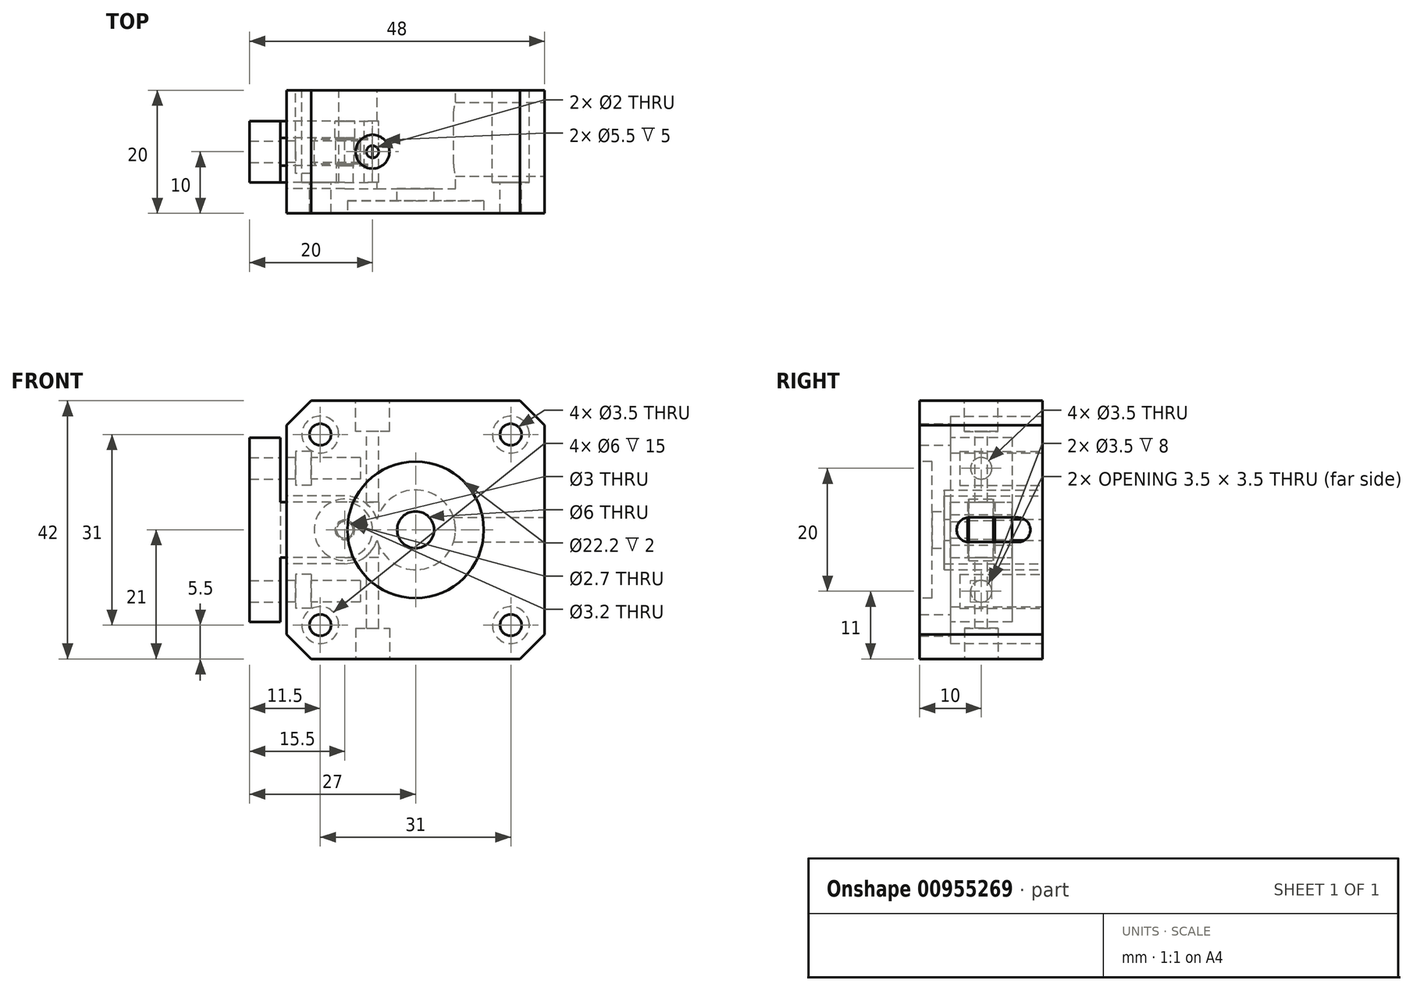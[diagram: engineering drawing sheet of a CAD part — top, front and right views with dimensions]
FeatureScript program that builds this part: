
annotation { "Feature Type Name" : "Feature", "Feature Type Description" : "" }
export const myFeature = defineFeature(function(context is Context, id is Id, definition is map)
    precondition{}
    {
        {
            var Q0;
            Q0=qCreatedBy(makeId("Front.planeOp"),FACE);
            var sketch = newSketch(context, id + "F0", { "sketchPlane" : qUnion([Q0])});
            skLineSegment(sketch, "E0.bottom", {"start": v(21, -21) * mm, "end": v(-21, -21) * mm});
            skLineSegment(sketch, "E0.top", {"start": v(21, 21) * mm, "end": v(-21, 21) * mm});
            skLineSegment(sketch, "E0.left", {"start": v(21, -21) * mm, "end": v(21, 21) * mm});
            skLineSegment(sketch, "E0.right", {"start": v(-21, -21) * mm, "end": v(-21, 21) * mm});
            skPoint(sketch, "E0.middle", {"position": v(0, 0) * mm});
            skLineSegment(sketch, "E1.bottom", {"start": v(15.5, -15.5) * mm, "end": v(-15.5, -15.5) * mm, "construction": true});
            skLineSegment(sketch, "E1.top", {"start": v(15.5, 15.5) * mm, "end": v(-15.5, 15.5) * mm, "construction": true});
            skLineSegment(sketch, "E1.left", {"start": v(15.5, -15.5) * mm, "end": v(15.5, 15.5) * mm, "construction": true});
            skLineSegment(sketch, "E1.right", {"start": v(-15.5, -15.5) * mm, "end": v(-15.5, 15.5) * mm, "construction": true});
            skCircle(sketch, "E2", {"center": v(-15.5, 15.5) * mm, "radius": 1.75 * mm});
            skCircle(sketch, "E3", {"center": v(15.5, 15.5) * mm, "radius": 1.75 * mm});
            skCircle(sketch, "E4", {"center": v(-15.5, -15.5) * mm, "radius": 1.75 * mm});
            skCircle(sketch, "E5", {"center": v(15.5, -15.5) * mm, "radius": 1.75 * mm});
            skCircle(sketch, "E6", {"center": v(0, 0) * mm, "radius": 3 * mm});
            skSolve(sketch);
        }
        {
            var Q0;
            Q0 = qSketchRegion(id + "F0", true);
            extrude(context, id + "F1", {"entities" : qUnion([Q0]), "endBound" : BoundingType.SYMMETRIC, "depth" : 20 * mm, "offsetDistance" : 25 * mm});
        }
        {
            var Q0;
            Q0=makeQuery(id+"F1.opExtrude","CAP_FACE",FACE,{"disambiguationData":[OSD([sQuery(id+"F0.wireOp",EDGE,"E0.bottom"),sQuery(id+"F0.wireOp",EDGE,"E0.top"),sQuery(id+"F0.wireOp",EDGE,"E0.left"),sQuery(id+"F0.wireOp",EDGE,"E0.right"),sQuery(id+"F0.wireOp",EDGE,"E2"),sQuery(id+"F0.wireOp",EDGE,"E3"),sQuery(id+"F0.wireOp",EDGE,"E4"),sQuery(id+"F0.wireOp",EDGE,"E5"),sQuery(id+"F0.wireOp",EDGE,"E6")])],"isStart":false});
            var sketch = newSketch(context, id + "F2", { "sketchPlane" : qUnion([Q0])});
            skCircle(sketch, "E7", {"center": v(0, 0) * mm, "radius": 11.1 * mm});
            skSolve(sketch);
        }
        {
            var Q0;
            Q0 = qSketchRegion(id + "F2", true);
            extrude(context, id + "F3", {"entities" : qUnion([Q0]), "operationType" : NewBodyOperationType.REMOVE, "oppositeDirection" : true, "depth" : 2 * mm, "offsetDistance" : 25 * mm});
        }
        {
            var Q0;
            Q0=makeQuery(id+"F1.opExtrude","SWEPT_FACE",FACE,{"disambiguationData":[OSD([sQuery(id+"F0.wireOp",EDGE,"E0.top")])]});
            var sketch = newSketch(context, id + "F4", { "sketchPlane" : qUnion([Q0])});
            skLineSegment(sketch, "E8", {"start": v(21, 10) * mm, "end": v(-21, -10) * mm, "construction": true});
            skLineSegment(sketch, "E9", {"start": v(0, 0) * mm, "end": v(-7, 0) * mm, "construction": true});
            skCircle(sketch, "E10", {"center": v(-7, 0) * mm, "radius": 1 * mm});
            skSolve(sketch);
        }
        {
            var Q0;
            Q0 = qSketchRegion(id + "F4", true);
            var Q1;
            Q1=makeQuery(id+"F1.opExtrude","SWEPT_FACE",FACE,{"disambiguationData":[OSD([sQuery(id+"F0.wireOp",EDGE,"E0.bottom")])]});
            extrude(context, id + "F5", {"entities" : qUnion([Q0]), "operationType" : NewBodyOperationType.REMOVE, "endBound" : BoundingType.UP_TO_SURFACE, "oppositeDirection" : true, "depth" : 25 * mm, "endBoundEntityFace" : qUnion([Q1]), "offsetDistance" : 25 * mm});
        }
        {
            var Q0;
            Q0=makeQuery(id+"F1.opExtrude","CAP_FACE",FACE,{"disambiguationData":[OSD([sQuery(id+"F0.wireOp",EDGE,"E0.bottom"),sQuery(id+"F0.wireOp",EDGE,"E0.top"),sQuery(id+"F0.wireOp",EDGE,"E0.left"),sQuery(id+"F0.wireOp",EDGE,"E0.right"),sQuery(id+"F0.wireOp",EDGE,"E2"),sQuery(id+"F0.wireOp",EDGE,"E3"),sQuery(id+"F0.wireOp",EDGE,"E4"),sQuery(id+"F0.wireOp",EDGE,"E5"),sQuery(id+"F0.wireOp",EDGE,"E6")])],"isStart":true});
            var sketch = newSketch(context, id + "F6", { "sketchPlane" : qUnion([Q0])});
            skCircle(sketch, "E11", {"center": v(0, 0) * mm, "radius": 6 * mm, "construction": true});
            skLineSegment(sketch, "E12", {"start": v(0, 0) * mm, "end": v(21, 0) * mm, "construction": true});
            skCircle(sketch, "E13", {"center": v(11.5, 0) * mm, "radius": 5 * mm, "construction": true});
            skArc(sketch, "E14.0", {"start": v(6.27, 1.7) * mm, "mid": v(-6.5, 0) * mm, "end": v(6.27, -1.7) * mm});
            skArc(sketch, "E15.0", {"start": v(11.5, 5.5) * mm, "mid": v(8.27, 4.45) * mm, "end": v(6.27, 1.7) * mm});
            skLineSegment(sketch, "E16", {"start": v(11.5, 5.5) * mm, "end": v(21, 5.5) * mm});
            skLineSegment(sketch, "E17", {"start": v(11.5, -5.5) * mm, "end": v(21, -5.5) * mm});
            skLineSegment(sketch, "E18", {"start": v(21, -5.5) * mm, "end": v(21, 5.5) * mm});
            skArc(sketch, "E19.trimOffspring", {"start": v(6.27, -1.7) * mm, "mid": v(8.27, -4.45) * mm, "end": v(11.5, -5.5) * mm});
            skSolve(sketch);
        }
        {
            var Q0;
            Q0 = qSketchRegion(id + "F6", true);
            extrude(context, id + "F7", {"entities" : qUnion([Q0]), "operationType" : NewBodyOperationType.REMOVE, "oppositeDirection" : true, "depth" : 16 * mm, "offsetDistance" : 25 * mm});
        }
        {
            var Q0;
            Q0=makeQuery(id+"F1.opExtrude","SWEPT_FACE",FACE,{"disambiguationData":[OSD([sQuery(id+"F0.wireOp",EDGE,"E0.right")])]});
            var sketch = newSketch(context, id + "F8", { "sketchPlane" : qUnion([Q0])});
            skCircle(sketch, "E20", {"center": v(0, 10) * mm, "radius": 1.75 * mm});
            skCircle(sketch, "E21", {"center": v(0, -10) * mm, "radius": 1.75 * mm});
            skLineSegment(sketch, "E22", {"start": v(0, 21) * mm, "end": v(0, 10) * mm, "construction": true});
            skLineSegment(sketch, "E23", {"start": v(0, 10) * mm, "end": v(0, -10) * mm, "construction": true});
            skLineSegment(sketch, "E24", {"start": v(0, -10) * mm, "end": v(0, -21) * mm, "construction": true});
            skSolve(sketch);
        }
        {
            var Q0;
            Q0 = qSketchRegion(id + "F8", true);
            var Q1;
            Q1=makeQuery(id+"F1.opExtrude","SWEPT_FACE",FACE,{"disambiguationData":[OSD([sQuery(id+"F0.wireOp",EDGE,"E0.left")])]});
            extrude(context, id + "F9", {"entities" : qUnion([Q0]), "operationType" : NewBodyOperationType.REMOVE, "oppositeDirection" : true, "depth" : 12 * mm, "endBoundEntityFace" : qUnion([Q1]), "offsetDistance" : 25 * mm});
        }
        {
            var Q0;
            Q0=qCreatedBy(makeId("Front.planeOp"),FACE);
            var sketch = newSketch(context, id + "F10", { "sketchPlane" : qUnion([Q0])});
            skCircle(sketch, "E25", {"center": v(-11.5, 0) * mm, "radius": 5 * mm});
            skCircle(sketch, "E26", {"center": v(-11.5, 0) * mm, "radius": 1.5 * mm});
            skSolve(sketch);
        }
        {
            var Q0;
            Q0 = qSketchRegion(id + "F10", true);
            extrude(context, id + "F11", {"entities" : qUnion([Q0]), "operationType" : NewBodyOperationType.ADD, "endBound" : BoundingType.SYMMETRIC, "depth" : 4 * mm, "offsetDistance" : 25 * mm});
        }
        {
            var Q0;
            Q0=makeQuery(id+"F1.opExtrude","SWEPT_FACE",FACE,{"disambiguationData":[OSD([sQuery(id+"F0.wireOp",EDGE,"E0.right")])]});
            cPlane(context, id + "F12", {"entities" : qUnion([Q0]), "cplaneType" : CPlaneType.OFFSET, "offset" : 1 * mm, "width" : 150 * mm, "height" : 150 * mm});
        }
        {
            var Q0;
            Q0=qCreatedBy(id+"F12.planeOp",FACE);
            var sketch = newSketch(context, id + "F13", { "sketchPlane" : qUnion([Q0])});
            skCircle(sketch, "E27", {"center": v(0, 10) * mm, "radius": 1.75 * mm});
            skCircle(sketch, "E28", {"center": v(0, -10) * mm, "radius": 1.75 * mm});
            skLineSegment(sketch, "E29.bottom", {"start": v(-5, 15) * mm, "end": v(5, 15) * mm});
            skLineSegment(sketch, "E29.top", {"start": v(-5, -15) * mm, "end": v(5, -15) * mm});
            skLineSegment(sketch, "E29.left", {"start": v(-5, 15) * mm, "end": v(-5, -15) * mm});
            skLineSegment(sketch, "E29.right", {"start": v(5, 15) * mm, "end": v(5, -15) * mm});
            skSolve(sketch);
        }
        {
            var Q0;
            Q0 = qSketchRegion(id + "F13", true);
            extrude(context, id + "F14", {"entities" : qUnion([Q0]), "depth" : 5 * mm, "offsetDistance" : 25 * mm});
        }
        {
            var Q0;
            Q0=makeQuery(id+"F14.opExtrude","CAP_FACE",FACE,{"disambiguationData":[OSD([sQuery(id+"F13.wireOp",EDGE,"E27"),sQuery(id+"F13.wireOp",EDGE,"E28"),sQuery(id+"F13.wireOp",EDGE,"E29.bottom"),sQuery(id+"F13.wireOp",EDGE,"E29.top"),sQuery(id+"F13.wireOp",EDGE,"E29.left"),sQuery(id+"F13.wireOp",EDGE,"E29.right")])],"isStart":true});
            var sketch = newSketch(context, id + "F15", { "sketchPlane" : qUnion([Q0])});
            skLineSegment(sketch, "E30", {"start": v(-5, 15) * mm, "end": v(5, -15) * mm, "construction": true});
            skLineSegment(sketch, "E31.bottom", {"start": v(-5, 4.5) * mm, "end": v(-2.25, 4.5) * mm});
            skLineSegment(sketch, "E31.top", {"start": v(-5, -4.5) * mm, "end": v(-2.25, -4.5) * mm});
            skLineSegment(sketch, "E31.left", {"start": v(-5, 4.5) * mm, "end": v(-5, -4.5) * mm});
            skLineSegment(sketch, "E31.right", {"start": v(-2.25, 4.5) * mm, "end": v(-2.25, -4.5) * mm});
            skLineSegment(sketch, "E32.bottom", {"start": v(2.25, 4.5) * mm, "end": v(5, 4.5) * mm});
            skLineSegment(sketch, "E32.top", {"start": v(2.25, -4.5) * mm, "end": v(5, -4.5) * mm});
            skLineSegment(sketch, "E32.left", {"start": v(2.25, 4.5) * mm, "end": v(2.25, -4.5) * mm});
            skLineSegment(sketch, "E32.right", {"start": v(5, 4.5) * mm, "end": v(5, -4.5) * mm});
            skLineSegment(sketch, "E33", {"start": v(0, 0) * mm, "end": v(-2.25, 0) * mm, "construction": true});
            skLineSegment(sketch, "E34", {"start": v(0, 0) * mm, "end": v(2.25, 0) * mm, "construction": true});
            skSolve(sketch);
        }
        {
            var Q0;
            Q0 = qSketchRegion(id + "F15", true);
            extrude(context, id + "F16", {"entities" : qUnion([Q0]), "operationType" : NewBodyOperationType.ADD, "depth" : 16 * mm, "offsetDistance" : 25 * mm});
        }
        {
            var Q0;
            Q0=makeQuery(id+"F16.boolean.opBoolean","MERGE",FACE,{"derivedFrom":[makeQuery(id+"F14.opExtrude","SWEPT_FACE",FACE,{"disambiguationData":[OSD([sQuery(id+"F13.wireOp",EDGE,"E29.left")])]}),makeQuery(id+"F16.opExtrude","SWEPT_FACE",FACE,{"disambiguationData":[OSD([sQuery(id+"F15.wireOp",EDGE,"E32.right")])]})]});
            var sketch = newSketch(context, id + "F17", { "sketchPlane" : qUnion([Q0])});
            skArc(sketch, "E35", {"start": v(11.5, 4.5) * mm, "mid": v(7, 0) * mm, "end": v(11.5, -4.5) * mm});
            skLineSegment(sketch, "E36", {"start": v(11.5, 4.5) * mm, "end": v(6, 4.5) * mm});
            skLineSegment(sketch, "E37", {"start": v(6, 4.5) * mm, "end": v(6, -4.5) * mm});
            skLineSegment(sketch, "E38", {"start": v(6, -4.5) * mm, "end": v(11.5, -4.5) * mm});
            skSolve(sketch);
        }
        {
            var Q0;
            Q0 = qSketchRegion(id + "F17", true);
            var Q1;
            Q1=makeQuery(id+"F16.boolean.opBoolean","MERGE",FACE,{"derivedFrom":[makeQuery(id+"F14.opExtrude","SWEPT_FACE",FACE,{"disambiguationData":[OSD([sQuery(id+"F13.wireOp",EDGE,"E29.right")])]}),makeQuery(id+"F16.opExtrude","SWEPT_FACE",FACE,{"disambiguationData":[OSD([sQuery(id+"F15.wireOp",EDGE,"E31.left")])]})]});
            extrude(context, id + "F18", {"entities" : qUnion([Q0]), "operationType" : NewBodyOperationType.REMOVE, "endBound" : BoundingType.UP_TO_SURFACE, "oppositeDirection" : true, "depth" : 25 * mm, "endBoundEntityFace" : qUnion([Q1]), "offsetDistance" : 25 * mm});
        }
        {
            var Q0;
            Q0=makeQuery(id+"F1.opExtrude","SWEPT_FACE",FACE,{"disambiguationData":[OSD([sQuery(id+"F0.wireOp",EDGE,"E0.top")])]});
            var sketch = newSketch(context, id + "F19", { "sketchPlane" : qUnion([Q0])});
            skCircle(sketch, "E39", {"center": v(-7, 0) * mm, "radius": 2.75 * mm});
            skSolve(sketch);
        }
        {
            var Q0;
            Q0 = qSketchRegion(id + "F19", true);
            extrude(context, id + "F20", {"entities" : qUnion([Q0]), "operationType" : NewBodyOperationType.REMOVE, "oppositeDirection" : true, "depth" : 5 * mm, "offsetDistance" : 25 * mm});
        }
        {
            var Q0;
            Q0=makeQuery(id+"F1.opExtrude","SWEPT_FACE",FACE,{"disambiguationData":[OSD([sQuery(id+"F0.wireOp",EDGE,"E0.bottom")])]});
            var sketch = newSketch(context, id + "F21", { "sketchPlane" : qUnion([Q0])});
            skCircle(sketch, "E40", {"center": v(-7, 0) * mm, "radius": 2.75 * mm});
            skSolve(sketch);
        }
        {
            var Q0;
            Q0 = qSketchRegion(id + "F21", true);
            extrude(context, id + "F22", {"entities" : qUnion([Q0]), "operationType" : NewBodyOperationType.REMOVE, "oppositeDirection" : true, "depth" : 5 * mm, "offsetDistance" : 25 * mm});
        }
        {
            var Q0;
            Q0=makeQuery(id+"F16.boolean.opBoolean","MERGE",FACE,{"derivedFrom":[makeQuery(id+"F14.opExtrude","SWEPT_FACE",FACE,{"disambiguationData":[OSD([sQuery(id+"F13.wireOp",EDGE,"E29.left")])]}),makeQuery(id+"F16.opExtrude","SWEPT_FACE",FACE,{"disambiguationData":[OSD([sQuery(id+"F15.wireOp",EDGE,"E32.right")])]})]});
            var sketch = newSketch(context, id + "F23", { "sketchPlane" : qUnion([Q0])});
            skCircle(sketch, "E41", {"center": v(11.5, 0) * mm, "radius": 1.35 * mm});
            skSolve(sketch);
        }
        {
            var Q0;
            Q0 = qSketchRegion(id + "F23", true);
            var Q1;
            Q1=makeQuery(id+"F16.boolean.opBoolean","MERGE",FACE,{"derivedFrom":[makeQuery(id+"F14.opExtrude","SWEPT_FACE",FACE,{"disambiguationData":[OSD([sQuery(id+"F13.wireOp",EDGE,"E29.right")])]}),makeQuery(id+"F16.opExtrude","SWEPT_FACE",FACE,{"disambiguationData":[OSD([sQuery(id+"F15.wireOp",EDGE,"E31.left")])]})]});
            extrude(context, id + "F24", {"entities" : qUnion([Q0]), "operationType" : NewBodyOperationType.REMOVE, "endBound" : BoundingType.UP_TO_SURFACE, "oppositeDirection" : true, "depth" : 25 * mm, "endBoundEntityFace" : qUnion([Q1]), "offsetDistance" : 25 * mm});
        }
        {
            var Q0;
            Q0=makeQuery(id+"F16.boolean.opBoolean","MERGE",FACE,{"derivedFrom":[makeQuery(id+"F14.opExtrude","SWEPT_FACE",FACE,{"disambiguationData":[OSD([sQuery(id+"F13.wireOp",EDGE,"E29.left")])]}),makeQuery(id+"F16.opExtrude","SWEPT_FACE",FACE,{"disambiguationData":[OSD([sQuery(id+"F15.wireOp",EDGE,"E32.right")])]})]});
            var sketch = newSketch(context, id + "F25", { "sketchPlane" : qUnion([Q0])});
            skCircle(sketch, "E42", {"center": v(11.5, 0) * mm, "radius": 1.6 * mm});
            skSolve(sketch);
        }
        {
            var Q0;
            Q0 = qSketchRegion(id + "F25", true);
            var Q1;
            Q1=makeQuery(id+"F16.opExtrude","SWEPT_FACE",FACE,{"disambiguationData":[OSD([sQuery(id+"F15.wireOp",EDGE,"E32.left")])]});
            extrude(context, id + "F26", {"entities" : qUnion([Q0]), "operationType" : NewBodyOperationType.REMOVE, "endBound" : BoundingType.UP_TO_SURFACE, "oppositeDirection" : true, "depth" : 25 * mm, "endBoundEntityFace" : qUnion([Q1]), "offsetDistance" : 25 * mm});
        }
        {
            var Q0;
            Q0=makeQuery(id+"F1.opExtrude","SWEPT_EDGE",EDGE,{"disambiguationData":[OSD([sQuery(id+"F0.wireOp",EDGE,"E0.top"),sQuery(id+"F0.wireOp",EDGE,"E0.left")])]});
            var Q1;
            Q1=makeQuery(id+"F1.opExtrude","SWEPT_EDGE",EDGE,{"disambiguationData":[OSD([sQuery(id+"F0.wireOp",EDGE,"E0.bottom"),sQuery(id+"F0.wireOp",EDGE,"E0.left")])]});
            var Q2;
            Q2=makeQuery(id+"F1.opExtrude","SWEPT_EDGE",EDGE,{"disambiguationData":[OSD([sQuery(id+"F0.wireOp",EDGE,"E0.bottom"),sQuery(id+"F0.wireOp",EDGE,"E0.right")])]});
            var Q3;
            Q3=makeQuery(id+"F1.opExtrude","SWEPT_EDGE",EDGE,{"disambiguationData":[OSD([sQuery(id+"F0.wireOp",EDGE,"E0.top"),sQuery(id+"F0.wireOp",EDGE,"E0.right")])]});
            chamfer(context, id + "F27", {"entities" : qUnion([Q0, Q1, Q2, Q3]), "width" : 4 * mm, "tangentPropagation" : true});
        }
        {
            var Q0;
            Q0=makeQuery(id+"F1.opExtrude","CAP_FACE",FACE,{"disambiguationData":[OSD([sQuery(id+"F0.wireOp",EDGE,"E0.bottom"),sQuery(id+"F0.wireOp",EDGE,"E0.top"),sQuery(id+"F0.wireOp",EDGE,"E0.left"),sQuery(id+"F0.wireOp",EDGE,"E0.right"),sQuery(id+"F0.wireOp",EDGE,"E2"),sQuery(id+"F0.wireOp",EDGE,"E3"),sQuery(id+"F0.wireOp",EDGE,"E4"),sQuery(id+"F0.wireOp",EDGE,"E5"),sQuery(id+"F0.wireOp",EDGE,"E6")])],"isStart":true});
            var sketch = newSketch(context, id + "F28", { "sketchPlane" : qUnion([Q0])});
            skLineSegment(sketch, "E43.bottom", {"start": v(17, 12.75) * mm, "end": v(19.5, 12.75) * mm});
            skLineSegment(sketch, "E43.top", {"start": v(17, 7.25) * mm, "end": v(19.5, 7.25) * mm});
            skLineSegment(sketch, "E43.left", {"start": v(17, 12.75) * mm, "end": v(17, 7.25) * mm});
            skLineSegment(sketch, "E43.right", {"start": v(19.5, 12.75) * mm, "end": v(19.5, 7.25) * mm});
            skLineSegment(sketch, "E44", {"start": v(17, 7.25) * mm, "end": v(19.5, 12.75) * mm, "construction": true});
            skLineSegment(sketch, "E45.bottom", {"start": v(17, -7.25) * mm, "end": v(19.5, -7.25) * mm});
            skLineSegment(sketch, "E45.top", {"start": v(17, -12.75) * mm, "end": v(19.5, -12.75) * mm});
            skLineSegment(sketch, "E45.left", {"start": v(17, -7.25) * mm, "end": v(17, -12.75) * mm});
            skLineSegment(sketch, "E45.right", {"start": v(19.5, -7.25) * mm, "end": v(19.5, -12.75) * mm});
            skLineSegment(sketch, "E46", {"start": v(17, -12.75) * mm, "end": v(19.5, -7.25) * mm, "construction": true});
            skLineSegment(sketch, "E47", {"start": v(18.25, -10) * mm, "end": v(18.25, 10) * mm, "construction": true});
            skLineSegment(sketch, "E48", {"start": v(21, -17) * mm, "end": v(19.5, -12.75) * mm, "construction": true});
            skLineSegment(sketch, "E49", {"start": v(21, 17) * mm, "end": v(19.5, 12.75) * mm, "construction": true});
            skSolve(sketch);
        }
        {
            var Q0;
            Q0 = qSketchRegion(id + "F28", true);
            extrude(context, id + "F29", {"entities" : qUnion([Q0]), "operationType" : NewBodyOperationType.REMOVE, "oppositeDirection" : true, "depth" : 13.5 * mm, "offsetDistance" : 25 * mm});
        }
        {
            var Q0;
            Q0=makeQuery(id+"F1.opExtrude","SWEPT_FACE",FACE,{"disambiguationData":[OSD([sQuery(id+"F0.wireOp",EDGE,"E0.left")])]});
            var sketch = newSketch(context, id + "F30", { "sketchPlane" : qUnion([Q0])});
            skLineSegment(sketch, "E50", {"start": v(-10, 0) * mm, "end": v(-2, 0) * mm, "construction": true});
            skLineSegment(sketch, "E51", {"start": v(-2, 0) * mm, "end": v(6, 0) * mm, "construction": true});
            skLineSegment(sketch, "E52", {"start": v(6, 0) * mm, "end": v(10, 0) * mm, "construction": true});
            skArc(sketch, "E53", {"start": v(-2, 2) * mm, "mid": v(-4, 0) * mm, "end": v(-2, -2) * mm});
            skArc(sketch, "E54", {"start": v(6, -2) * mm, "mid": v(8, 0) * mm, "end": v(6, 2) * mm});
            skLineSegment(sketch, "E55", {"start": v(-2, 2) * mm, "end": v(6, 2) * mm});
            skLineSegment(sketch, "E56", {"start": v(-2, -2) * mm, "end": v(6, -2) * mm});
            skSolve(sketch);
        }
        {
            var Q0;
            Q0 = qSketchRegion(id + "F30", true);
            var Q1;
            Q1=makeQuery(id+"F7.boolean.opBoolean","COPY",FACE,{"derivedFrom":makeQuery(id+"F7.opExtrude","SWEPT_FACE",FACE,{"disambiguationData":[OSD([sQuery(id+"F6.wireOp",EDGE,"E14.0")])]})});
            extrude(context, id + "F31", {"entities" : qUnion([Q0]), "operationType" : NewBodyOperationType.REMOVE, "endBound" : BoundingType.UP_TO_SURFACE, "oppositeDirection" : true, "depth" : 25 * mm, "endBoundEntityFace" : qUnion([Q1]), "offsetDistance" : 25 * mm});
        }
        {
            var Q0;
            Q0=makeQuery(id+"F1.opExtrude","CAP_FACE",FACE,{"disambiguationData":[OSD([sQuery(id+"F0.wireOp",EDGE,"E0.bottom"),sQuery(id+"F0.wireOp",EDGE,"E0.top"),sQuery(id+"F0.wireOp",EDGE,"E0.left"),sQuery(id+"F0.wireOp",EDGE,"E0.right"),sQuery(id+"F0.wireOp",EDGE,"E2"),sQuery(id+"F0.wireOp",EDGE,"E3"),sQuery(id+"F0.wireOp",EDGE,"E4"),sQuery(id+"F0.wireOp",EDGE,"E5"),sQuery(id+"F0.wireOp",EDGE,"E6")])],"isStart":true});
            var sketch = newSketch(context, id + "F32", { "sketchPlane" : qUnion([Q0])});
            skCircle(sketch, "E57", {"center": v(-15.5, 15.5) * mm, "radius": 3 * mm});
            skCircle(sketch, "E58", {"center": v(15.5, 15.5) * mm, "radius": 3 * mm});
            skCircle(sketch, "E59", {"center": v(-15.5, -15.5) * mm, "radius": 3 * mm});
            skCircle(sketch, "E60", {"center": v(15.5, -15.5) * mm, "radius": 3 * mm});
            skSolve(sketch);
        }
        {
            var Q0;
            Q0 = qSketchRegion(id + "F32", true);
            extrude(context, id + "F33", {"entities" : qUnion([Q0]), "operationType" : NewBodyOperationType.REMOVE, "oppositeDirection" : true, "depth" : 15 * mm, "offsetDistance" : 25 * mm});
        }
    });
